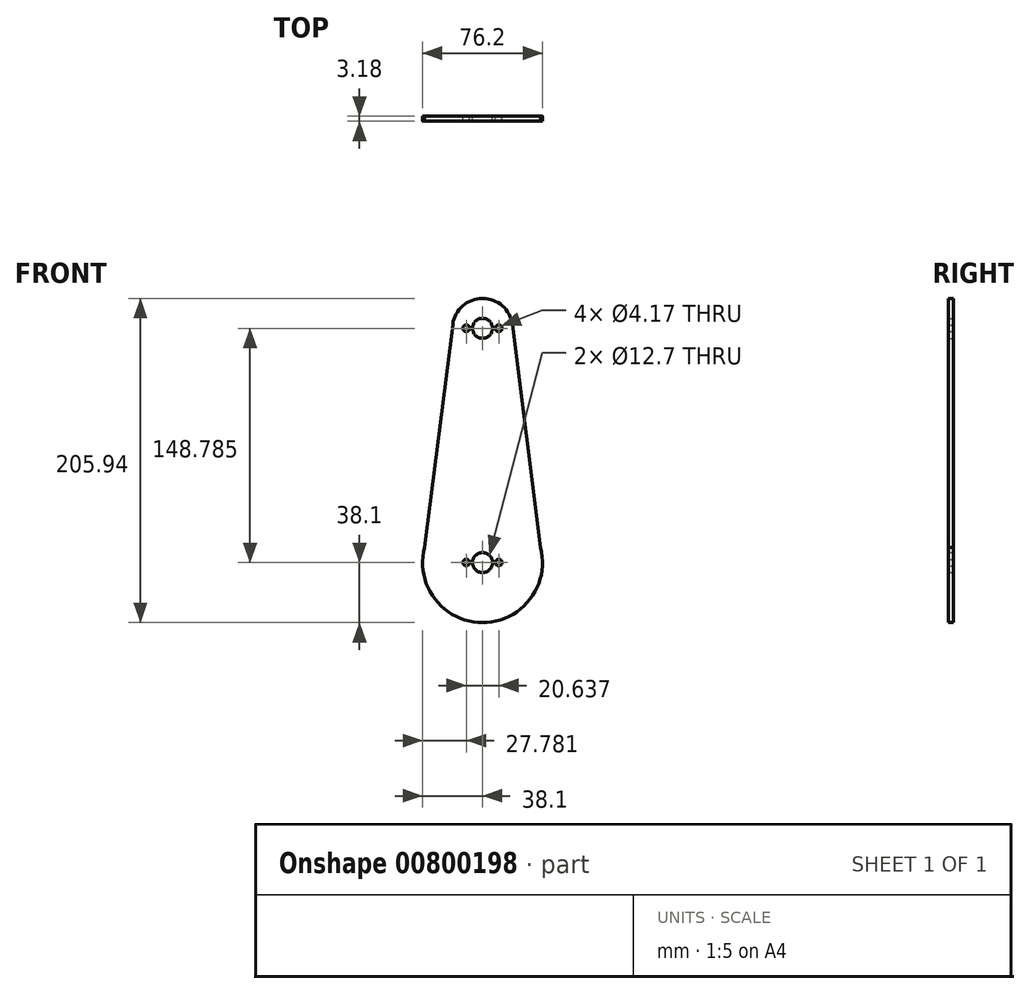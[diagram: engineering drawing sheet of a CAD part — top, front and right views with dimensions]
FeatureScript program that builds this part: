
annotation { "Feature Type Name" : "Feature", "Feature Type Description" : "" }
export const myFeature = defineFeature(function(context is Context, id is Id, definition is map)
    precondition{}
    {
        {
            var Q0;
            Q0=qCreatedBy(makeId("Front.planeOp"),FACE);
            var sketch = newSketch(context, id + "F0", { "sketchPlane" : qUnion([Q0])});
            skCircle(sketch, "E0", {"center": v(0, 0) * mm, "radius": 38.1 * mm});
            skCircle(sketch, "E1", {"center": v(0, 148.79) * mm, "radius": 19.05 * mm});
            skLineSegment(sketch, "E2", {"start": v(-38.1, 0) * mm, "end": v(-18.9, 151.19) * mm});
            skLineSegment(sketch, "E3", {"start": v(38.1, 0) * mm, "end": v(18.9, 151.19) * mm});
            skCircle(sketch, "E4", {"center": v(0, 148.79) * mm, "radius": 6.35 * mm});
            skCircle(sketch, "E5", {"center": v(0, 0) * mm, "radius": 6.35 * mm});
            skCircle(sketch, "E6", {"center": v(-10.32, 0) * mm, "radius": 2.08 * mm});
            skCircle(sketch, "E7", {"center": v(10.32, 0) * mm, "radius": 2.08 * mm});
            skCircle(sketch, "E8", {"center": v(-10.32, 148.79) * mm, "radius": 2.08 * mm});
            skCircle(sketch, "E9", {"center": v(10.32, 148.79) * mm, "radius": 2.08 * mm});
            skSolve(sketch);
        }
        {
            var Q0;
            Q0 = qSketchRegion(id + "F0", true);
            extrude(context, id + "F1", {"entities" : qUnion([Q0]), "depth" : 3.17 * mm, "offsetDistance" : 25.4 * mm});
        }
    });
